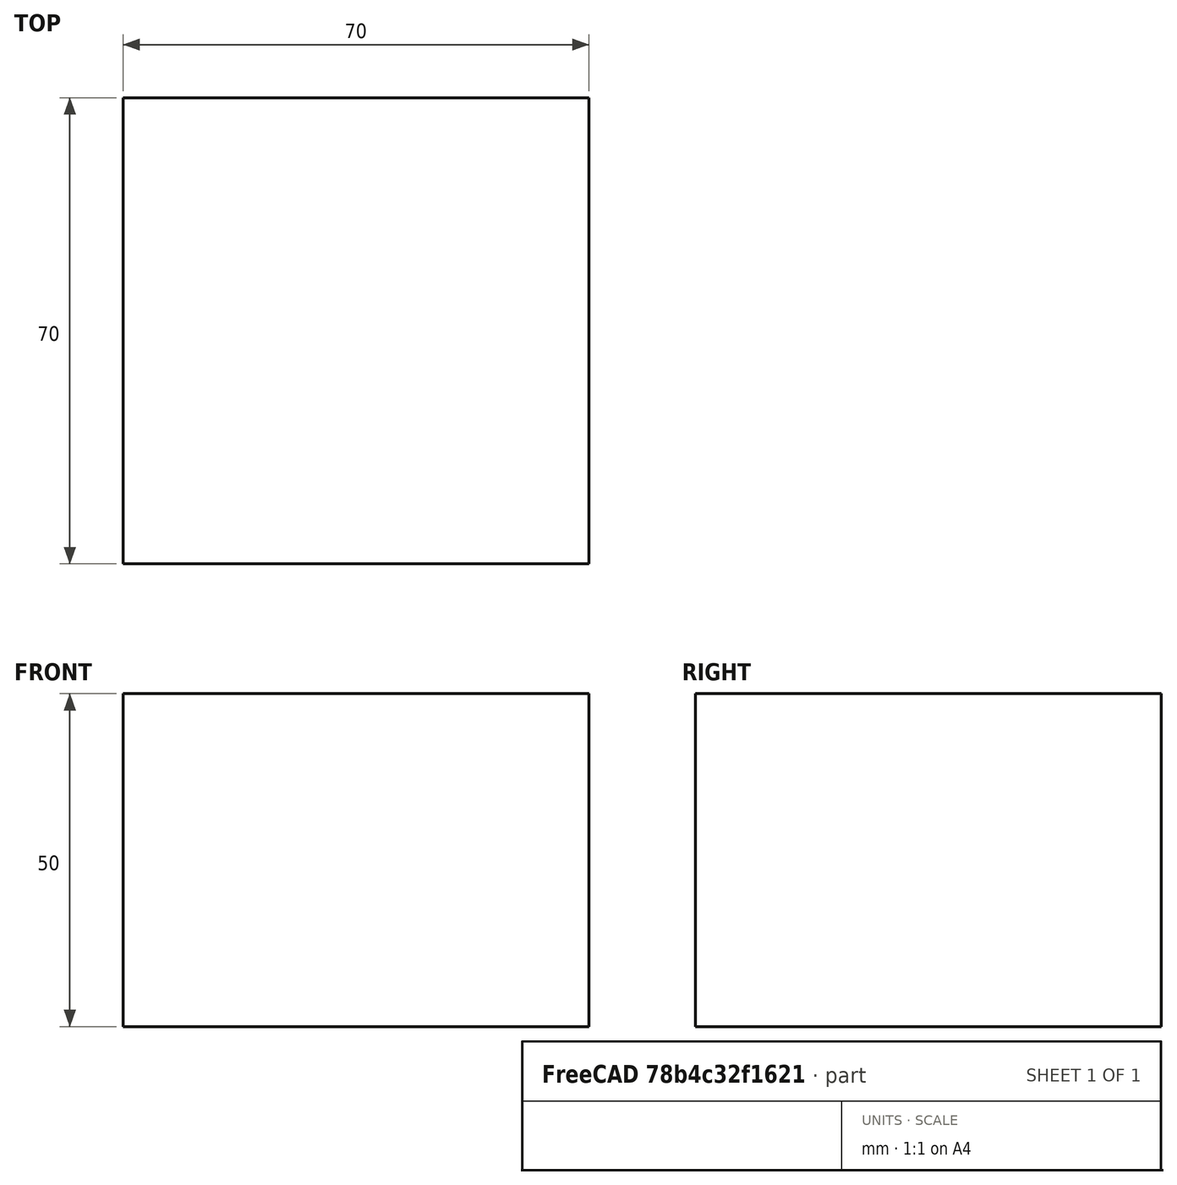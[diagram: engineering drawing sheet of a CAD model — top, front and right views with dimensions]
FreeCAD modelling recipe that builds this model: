
FCSTD DOCUMENT  (FreeCAD 0.15R4671 (Git))
Label: Square Bar 70 EN10059 S235JR
License: All rights reserved
LicenseURL: http://en.wikipedia.org/wiki/All_rights_reserved
objects: Sketcher::SketchObject×1, Part::Extrusion×1
note: 2 computed .brp shape members not serialized (recipe doc carries the construction recipe); baked Part::Feature solids carry a one-line shape summary decoded from their .brp

FEATURE [Sketcher::SketchObject] Sketch
  sketch-geometry (4):
    g0: LineSegment StartX=-35 StartY=-35 StartZ=0 EndX=35 EndY=-35 EndZ=0
    g1: LineSegment StartX=35 StartY=-35 StartZ=0 EndX=35 EndY=35 EndZ=0
    g2: LineSegment StartX=35 StartY=35 StartZ=0 EndX=-35 EndY=35 EndZ=0
    g3: LineSegment StartX=-35 StartY=35 StartZ=0 EndX=-35 EndY=-35 EndZ=0
  constraints (12):
    c: Coincident(g0,g1)
    c: Coincident(g1,g2)
    c: Coincident(g2,g3)
    c: Coincident(g3,g0)
    c: Horizontal(g0)
    c: Horizontal(g2)
    c: Vertical(g1)
    c: Vertical(g3)
    c: Symmetric(g1,g0,g-1)
    c: Symmetric(g2,g1,g-2)
    c: Equal(g1,g2)
    c: DistanceY(g1) = 70
FEATURE [Part::Extrusion] Extrude  label="Square Bar 70 EN10059 S235JR"
  Base = -> Sketch
  Dir = (0,0,50)
  Solid = true
